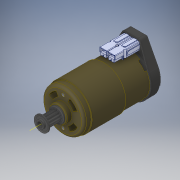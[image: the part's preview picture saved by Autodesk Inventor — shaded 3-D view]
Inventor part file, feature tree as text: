
AUTODESK INVENTOR PART (.ipt)
format: ipt  version: 2019.4 (Build 234330000, 330)  size: 5,931,008 bytes
history: native  units: in
note: dims shown in document units (in); Inventor stores cm internally (conversion verified against a paired STEP export)
features: other x13, plane x1
ambient origin geometry x8: Origin, YZ Plane, XZ Plane, XY Plane, X Axis, Y Axis, Z Axis, Center Point
bodies: Solid1 (feature_tree), Solid2 (feature_tree), Solid3 (feature_tree), Solid4 (feature_tree), Solid5 (feature_tree), Solid6 (feature_tree), Solid7 (feature_tree), Solid8 (feature_tree), Solid9 (feature_tree), Solid10 (feature_tree), Solid11 (feature_tree), Solid12 (feature_tree), Solid13 (feature_tree)
feature tree (14):
  plane  "Work Plane1"
  other  "217-4347-000 Rev2_1:1"
  other  "217-6457-001 Rev4_4:1"
  other  "217-6457-901 Rev3_Instruction Config_11:1"
  other  "30-45BBS Rev1_SHORTENED CONTACT_12:1"
  other  "30-45BBS Rev1_SHORTENED CONTACT_13:1"
  other  "PA45XX-X Rev1_14:1"
  other  "PA45XX-X Rev1_15:1"
  other  "217-6457-002 Rev7_6:1"
  other  "217-9191-008 Rev1_7:1"
  other  "217-9191-008 Rev1_8:1"
  other  "217-9191-008 Rev1_9:1"
  other  "217-9191-008 Rev1_10:1"
  other  "217-5871-001 Rev4_3:1"
